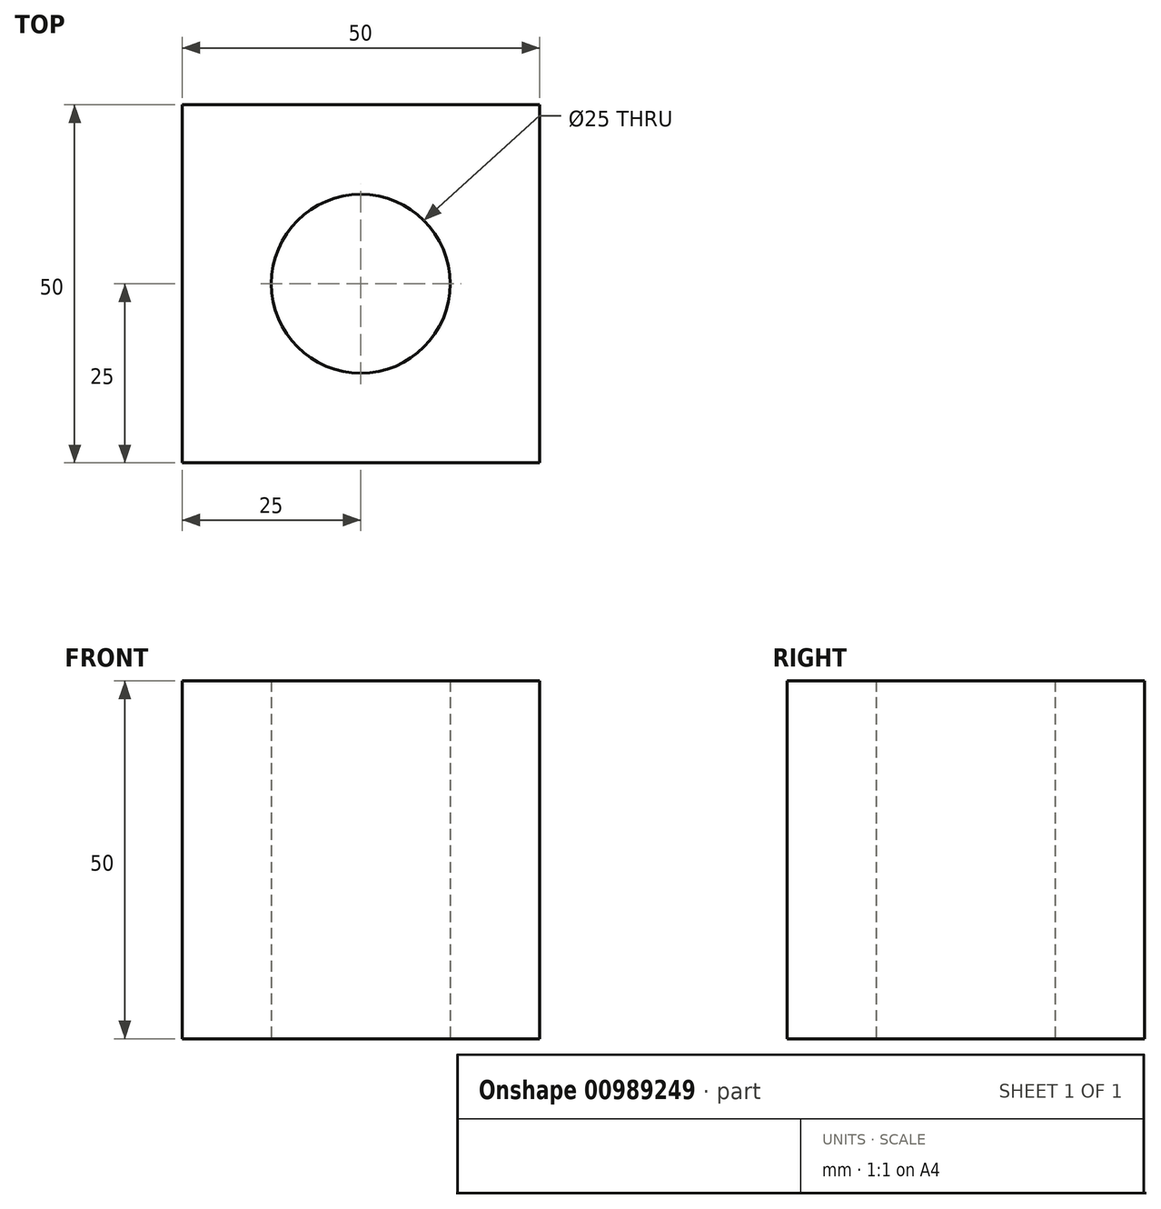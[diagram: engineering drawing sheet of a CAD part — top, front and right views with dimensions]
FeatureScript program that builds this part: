
annotation { "Feature Type Name" : "Feature", "Feature Type Description" : "" }
export const myFeature = defineFeature(function(context is Context, id is Id, definition is map)
    precondition{}
    {
        {
            var Q0;
            Q0=qCreatedBy(makeId("Top.planeOp"),FACE);
            var sketch = newSketch(context, id + "F0", { "sketchPlane" : qUnion([Q0])});
            skLineSegment(sketch, "E0", {"start": v(0, 0) * mm, "end": v(0, 50) * mm});
            skLineSegment(sketch, "E1", {"start": v(0, 50) * mm, "end": v(50, 50) * mm});
            skLineSegment(sketch, "E2", {"start": v(50, 50) * mm, "end": v(50, 0) * mm});
            skLineSegment(sketch, "E3", {"start": v(0, 0) * mm, "end": v(50, 0) * mm});
            skCircle(sketch, "E4", {"center": v(25, 25) * mm, "radius": 12.5 * mm});
            skLineSegment(sketch, "E5", {"start": v(0, 0) * mm, "end": v(50, 50) * mm, "construction": true});
            skSolve(sketch);
        }
        {
            var Q0;
            Q0=makeQuery(id+"F0.imprint","IMPRINT",FACE,{"disambiguationData":[TD([[makeQuery(id+"F0.imprint","IMPRINT",EDGE,{"derivedFrom":sQuery(id+"F0.wireOp",EDGE,"E0")}),-1.0]])]});
            extrude(context, id + "F1", {"entities" : qUnion([Q0]), "depth" : 50 * mm, "offsetDistance" : 25 * mm});
        }
    });
